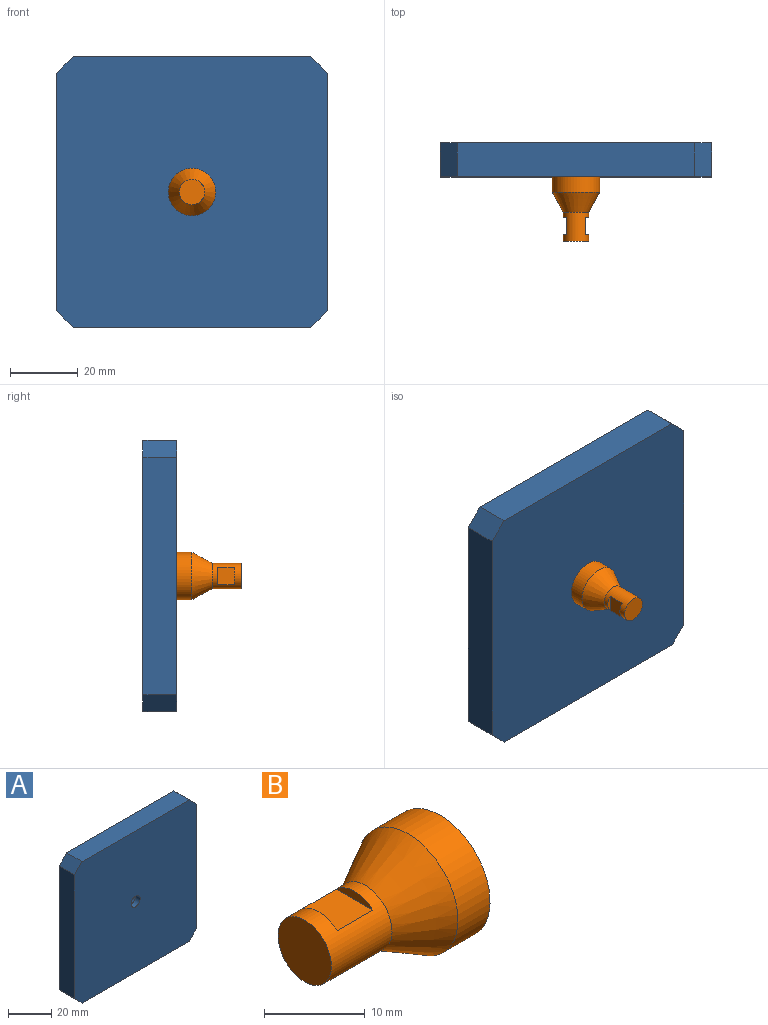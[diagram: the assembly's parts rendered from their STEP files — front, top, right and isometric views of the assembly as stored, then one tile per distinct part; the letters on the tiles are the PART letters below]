
ASSEMBLY  parts=2 mates=1
PART A: 13 faces, bbox 80x10x80 mm
  f0: cylinder r=3mm len=6mm, axis (0,-1,0), area 56.5mm2, adj f5,f11
  f1: plane 70x10mm, normal (0,0,1), area 700mm2, adj f5,f6,f8,f10
  f2: plane 70x10mm, normal (-1,0,0), area 700mm2, adj f5,f6,f7,f8
  f3: plane 70x10mm, normal (0,0,-1), area 700mm2, adj f5,f6,f7,f9
  f4: plane 70x10mm, normal (1,0,0), area 700mm2, adj f5,f6,f9,f10
  f5: plane 80x80mm, normal (0,-1,0), area 6321.7mm2, adj f0,f1,f2,f3,f4,f7,f8,f9
  f6: plane 80x80mm, normal (0,1,0), area 6271.5mm2, adj f1,f2,f3,f4,f7,f8,f9,f10
  f7: plane 10x5mm, normal (-0.71,0,-0.71), area 70.7mm2, adj f2,f3,f5,f6
  f8: plane 10x5mm, normal (-0.71,0,0.71), area 70.7mm2, adj f1,f2,f5,f6
  f9: plane 10x5mm, normal (0.71,0,-0.71), area 70.7mm2, adj f3,f4,f5,f6
  f10: plane 10x5mm, normal (0.71,0,0.71), area 70.7mm2, adj f1,f4,f5,f6
  f11: plane 10x10mm, normal (0,1,0), area 50.3mm2, adj f0,f12
  f12: cylinder r=5mm len=10mm, axis (0,1,0), area 219.9mm2, adj f6,f11
PART B: 13 faces, bbox 19x14x14 mm
  f0: cylinder r=3.75mm len=8.5mm, axis (-1,0,0), area 144.2mm2, adj f1,f4,f5,f6,f7,f8,f9,f10
  f1: plane 7.5x7.5mm, normal (-1,0,0), area 44.2mm2, adj f0
  f2: plane 14x14mm, normal (1,0,0), area 134.3mm2, adj f3,f11
  f3: cylinder r=7mm len=14mm, axis (-1,0,0), area 197.9mm2, adj f2,f4
  f4: cone r=3.75mm half-angle=28.4deg, axis (1,0,0), area 230.4mm2, adj f0,f3
  f5: plane 5.1x1mm, normal (1,0,0), area 3.5mm2, adj f0,f6
  f6: plane 5.1x5mm, normal (0,0,1), area 25.5mm2, adj f0,f5,f7
  f7: plane 5.1x1mm, normal (-1,0,0), area 3.5mm2, adj f0,f6
  f8: plane 5.1x1mm, normal (-1,0,0), area 3.5mm2, adj f0,f9
  f9: plane 5.1x5mm, normal (0,0,-1), area 25.5mm2, adj f0,f8,f10
  f10: plane 5.1x1mm, normal (1,0,0), area 3.5mm2, adj f0,f9
  f11: cylinder r=2.5mm len=10mm, axis (1,0,0), area 157.1mm2, adj f2,f12
  f12: plane 5x5mm, normal (1,0,0), area 19.6mm2, adj f11
PLACE A t=(-14,-2.7,0.57)mm
PLACE B rot(axis=(-0.58,-0.58,0.58),120deg) t=(-14,-18.69,0.57)mm
MATE parallel B.f11 <-> A.f0  axis (0,1,0) through (-14,-12.7,0.57)mm
